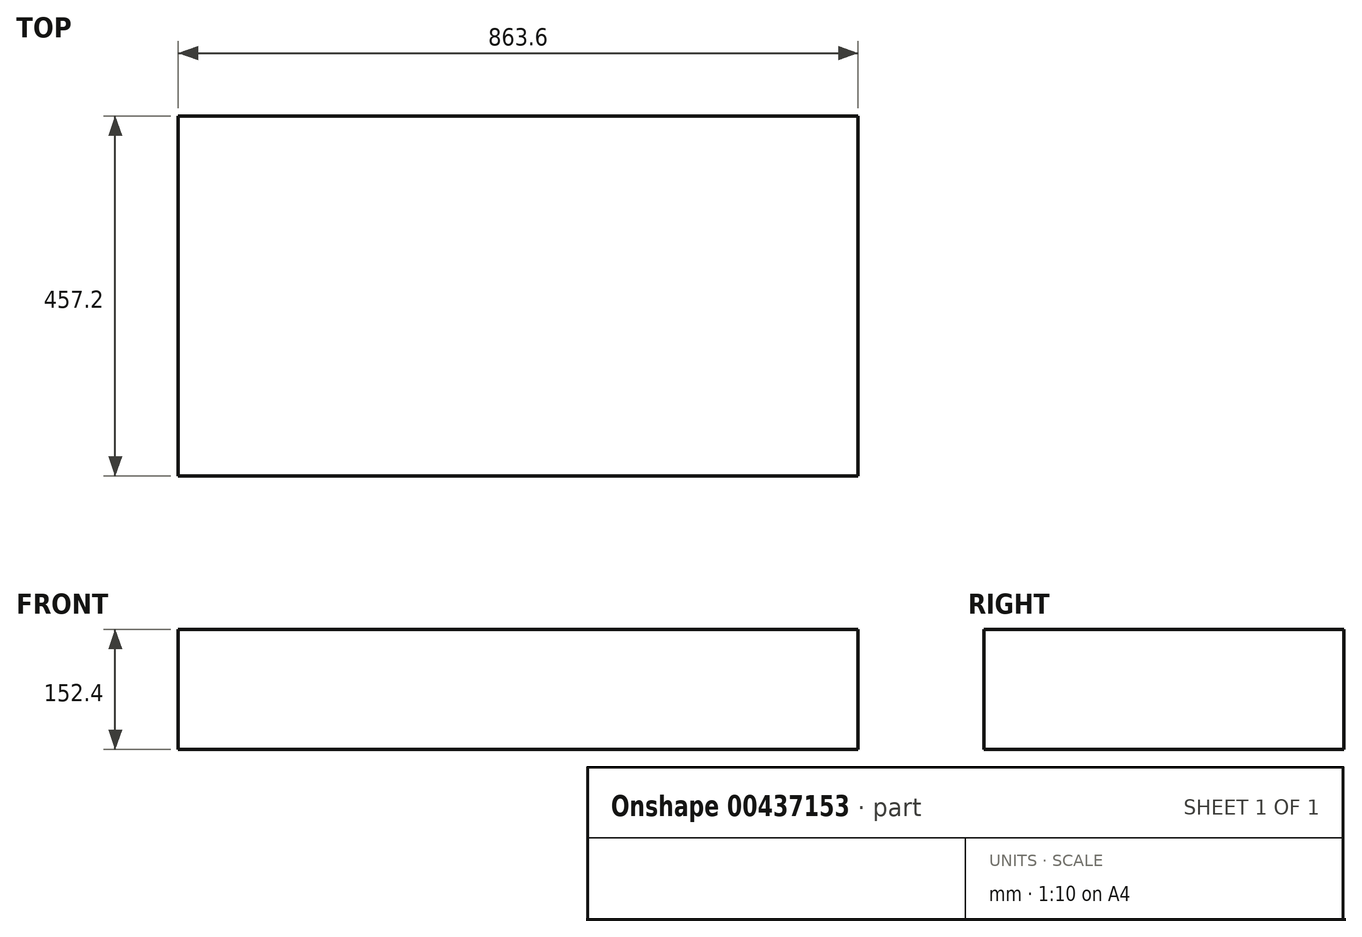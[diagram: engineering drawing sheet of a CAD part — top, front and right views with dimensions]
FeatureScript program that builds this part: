
annotation { "Feature Type Name" : "Feature", "Feature Type Description" : "" }
export const myFeature = defineFeature(function(context is Context, id is Id, definition is map)
    precondition{}
    {
        {
            var Q0;
            Q0=qCreatedBy(makeId("Front.planeOp"),FACE);
            var sketch = newSketch(context, id + "F0", { "sketchPlane" : qUnion([Q0])});
            skLineSegment(sketch, "E0.bottom", {"start": v(0, 0) * mm, "end": v(-863.6, 0) * mm});
            skLineSegment(sketch, "E0.top", {"start": v(0, 152.4) * mm, "end": v(-863.6, 152.4) * mm});
            skLineSegment(sketch, "E0.left", {"start": v(0, 0) * mm, "end": v(0, 152.4) * mm});
            skLineSegment(sketch, "E0.right", {"start": v(-863.6, 0) * mm, "end": v(-863.6, 152.4) * mm});
            skSolve(sketch);
        }
        {
            var Q0;
            Q0 = qSketchRegion(id + "F0", true);
            extrude(context, id + "F1", {"entities" : qUnion([Q0]), "depth" : 457.2 * mm});
        }
    });
